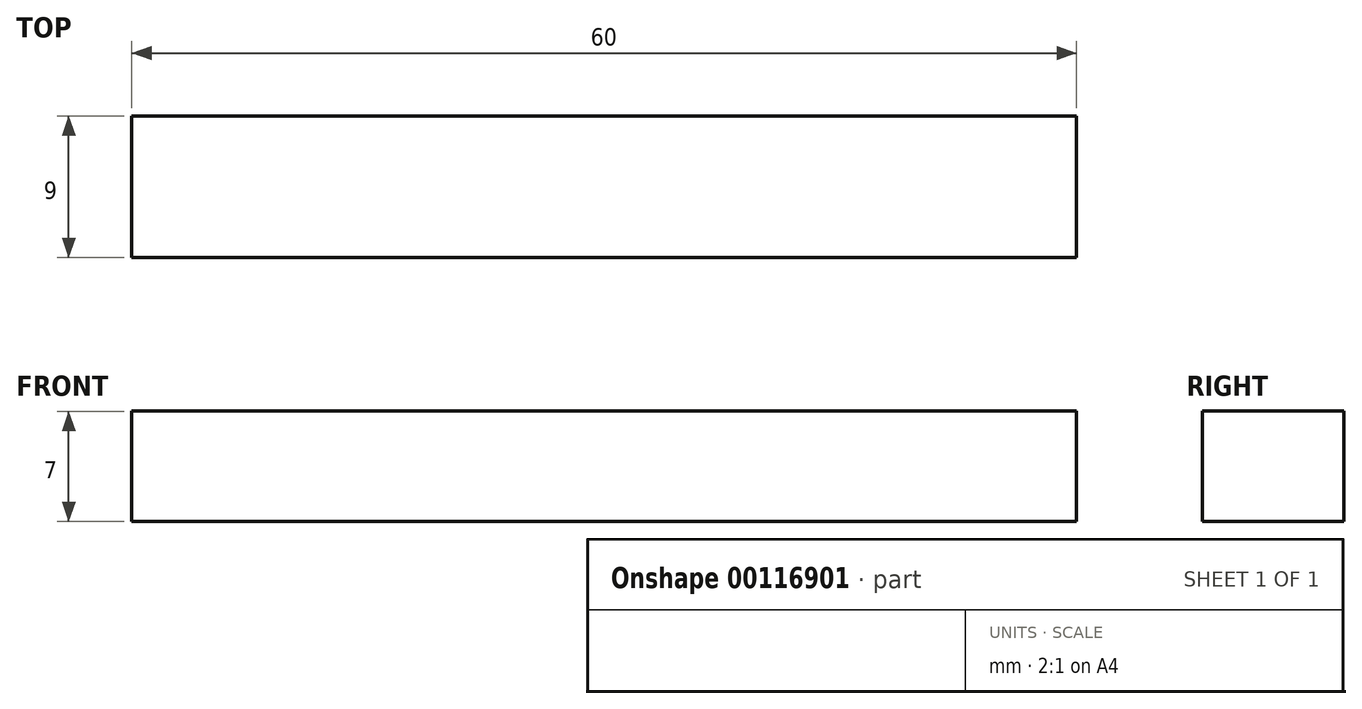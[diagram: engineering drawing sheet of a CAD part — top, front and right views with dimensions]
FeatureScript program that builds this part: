
annotation { "Feature Type Name" : "Feature", "Feature Type Description" : "" }
export const myFeature = defineFeature(function(context is Context, id is Id, definition is map)
    precondition{}
    {
        {
            var Q0;
            Q0=qCreatedBy(makeId("Front.planeOp"),FACE);
            var sketch = newSketch(context, id + "F0", { "sketchPlane" : qUnion([Q0])});
            skLineSegment(sketch, "E0.bottom", {"start": v(-40.3, 20.01) * mm, "end": v(19.7, 20.01) * mm});
            skLineSegment(sketch, "E0.top", {"start": v(-40.3, 13.01) * mm, "end": v(19.7, 13.01) * mm});
            skLineSegment(sketch, "E0.left", {"start": v(-40.3, 20.01) * mm, "end": v(-40.3, 13.01) * mm});
            skLineSegment(sketch, "E0.right", {"start": v(19.7, 20.01) * mm, "end": v(19.7, 13.01) * mm});
            skSolve(sketch);
        }
        {
            var Q0;
            Q0=makeQuery(id+"F0.imprint","IMPRINT",FACE,{"disambiguationData":[TD([[makeQuery(id+"F0.imprint","IMPRINT",EDGE,{"derivedFrom":sQuery(id+"F0.wireOp",EDGE,"E0.bottom")}),-1.0]])]});
            extrude(context, id + "F1", {"entities" : qUnion([Q0]), "depth" : 9 * mm});
        }
    });
